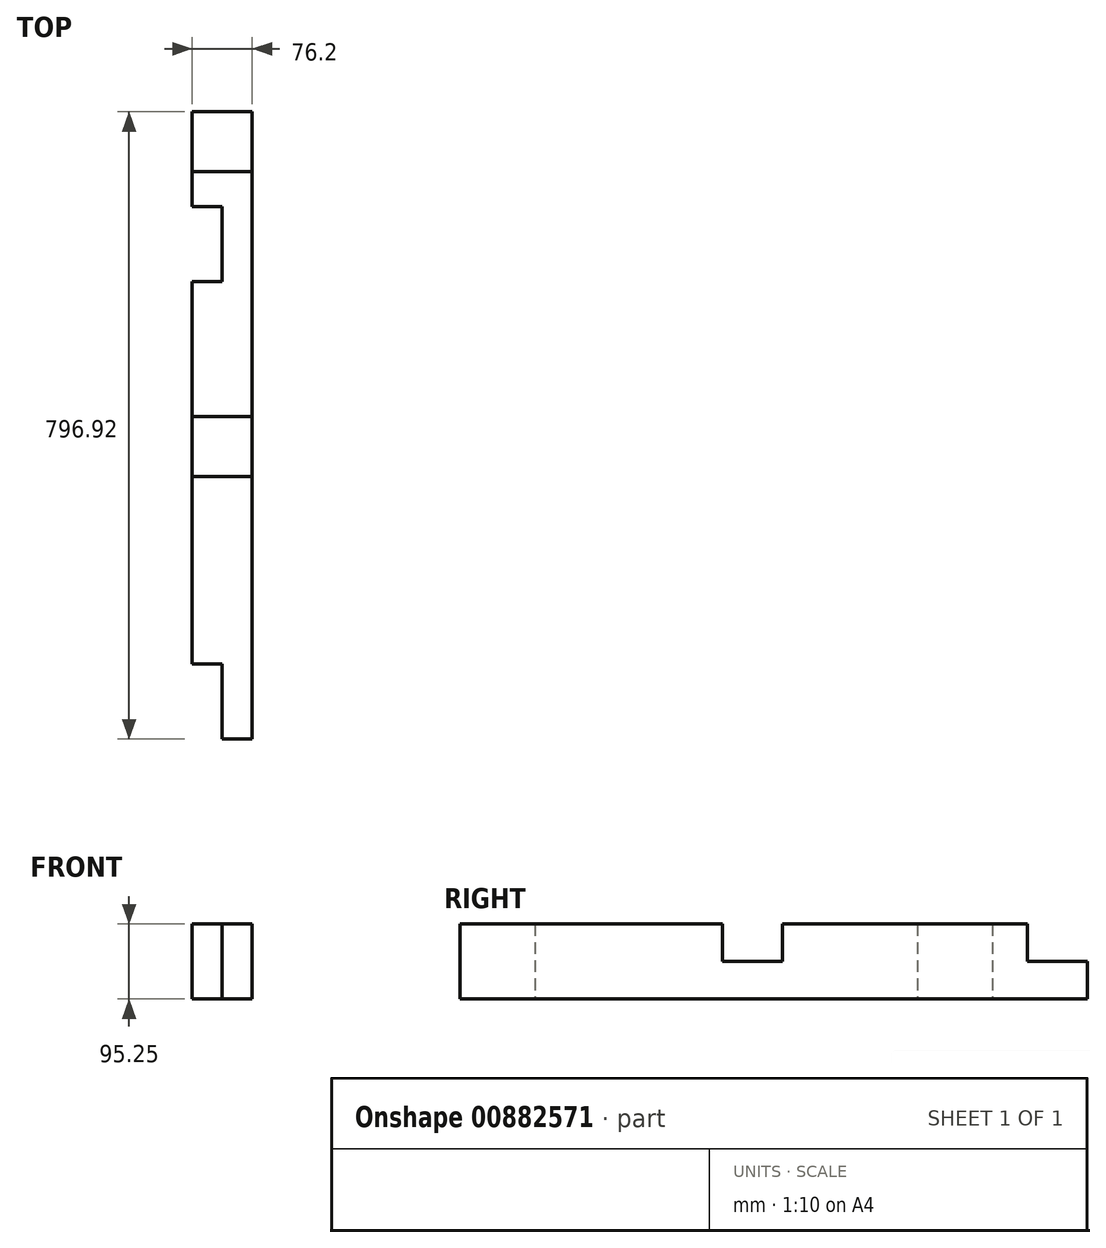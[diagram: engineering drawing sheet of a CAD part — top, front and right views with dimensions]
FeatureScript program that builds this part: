
annotation { "Feature Type Name" : "Feature", "Feature Type Description" : "" }
export const myFeature = defineFeature(function(context is Context, id is Id, definition is map)
    precondition{}
    {
        {
            var Q0;
            Q0=qCreatedBy(makeId("Front.planeOp"),FACE);
            var sketch = newSketch(context, id + "F0", { "sketchPlane" : qUnion([Q0])});
            skLineSegment(sketch, "E0.bottom", {"start": v(0, 0) * mm, "end": v(76.2, 0) * mm});
            skLineSegment(sketch, "E0.top", {"start": v(0, 95.25) * mm, "end": v(76.2, 95.25) * mm});
            skLineSegment(sketch, "E0.left", {"start": v(0, 0) * mm, "end": v(0, 95.25) * mm});
            skLineSegment(sketch, "E0.right", {"start": v(76.2, 0) * mm, "end": v(76.2, 95.25) * mm});
            skSolve(sketch);
        }
        {
            var Q0;
            Q0=qSketchRegion(id+"F0",true);
            extrude(context, id + "F1", {"entities" : qUnion([Q0]), "depth" : 796.92 * mm, "offsetDistance" : 25.4 * mm});
        }
        {
            var Q0;
            Q0=makeQuery(id+"F1.opExtrude","SWEPT_FACE",FACE,{"disambiguationData":[OSD([sQuery(id+"F0.wireOp",EDGE,"E0.right")])]});
            var sketch = newSketch(context, id + "F2", { "sketchPlane" : qUnion([Q0])});
            skLineSegment(sketch, "E1.bottom", {"start": v(-463.55, 95.25) * mm, "end": v(-387.35, 95.25) * mm});
            skLineSegment(sketch, "E1.top", {"start": v(-463.55, 47.62) * mm, "end": v(-387.35, 47.62) * mm});
            skLineSegment(sketch, "E1.left", {"start": v(-463.55, 95.25) * mm, "end": v(-463.55, 47.63) * mm});
            skLineSegment(sketch, "E1.right", {"start": v(-387.35, 95.25) * mm, "end": v(-387.35, 47.63) * mm});
            skLineSegment(sketch, "E2.bottom", {"start": v(-76.2, 95.25) * mm, "end": v(0, 95.25) * mm});
            skLineSegment(sketch, "E2.top", {"start": v(-76.2, 47.62) * mm, "end": v(0, 47.62) * mm});
            skLineSegment(sketch, "E2.left", {"start": v(-76.2, 95.25) * mm, "end": v(-76.2, 47.62) * mm});
            skLineSegment(sketch, "E2.right", {"start": v(0, 95.25) * mm, "end": v(0, 47.62) * mm});
            skSolve(sketch);
        }
        {
            var Q0;
            Q0=qSketchRegion(id+"F2",true);
            extrude(context, id + "F3", {"entities" : qUnion([Q0]), "operationType" : NewBodyOperationType.REMOVE, "endBound" : BoundingType.THROUGH_ALL, "oppositeDirection" : true, "depth" : 25.4 * mm, "offsetDistance" : 25.4 * mm});
        }
        {
            var Q0;
            Q0=makeQuery(id+"F1.opExtrude","SWEPT_FACE",FACE,{"disambiguationData":[OSD([sQuery(id+"F0.wireOp",EDGE,"E0.left")])]});
            var sketch = newSketch(context, id + "F4", { "sketchPlane" : qUnion([Q0])});
            skLineSegment(sketch, "E3.bottom", {"start": v(796.93, 95.25) * mm, "end": v(701.68, 95.25) * mm});
            skLineSegment(sketch, "E3.top", {"start": v(796.93, 0) * mm, "end": v(701.68, 0) * mm});
            skLineSegment(sketch, "E3.left", {"start": v(796.93, 95.25) * mm, "end": v(796.93, 0) * mm});
            skLineSegment(sketch, "E3.right", {"start": v(701.68, 95.25) * mm, "end": v(701.68, 0) * mm});
            skSolve(sketch);
        }
        {
            var Q0;
            Q0 = qSketchRegion(id + "F4", true);
            extrude(context, id + "F5", {"entities" : qUnion([Q0]), "operationType" : NewBodyOperationType.REMOVE, "oppositeDirection" : true, "depth" : 38.1 * mm, "offsetDistance" : 25.4 * mm});
        }
        {
            var Q0;
            Q0=makeQuery(id+"F1.opExtrude","SWEPT_FACE",FACE,{"disambiguationData":[OSD([sQuery(id+"F0.wireOp",EDGE,"E0.left")])]});
            var sketch = newSketch(context, id + "F6", { "sketchPlane" : qUnion([Q0])});
            skLineSegment(sketch, "E4.bottom", {"start": v(120.65, 95.25) * mm, "end": v(215.9, 95.25) * mm});
            skLineSegment(sketch, "E4.top", {"start": v(120.65, 0) * mm, "end": v(215.9, 0) * mm});
            skLineSegment(sketch, "E4.left", {"start": v(120.65, 95.25) * mm, "end": v(120.65, 0) * mm});
            skLineSegment(sketch, "E4.right", {"start": v(215.9, 95.25) * mm, "end": v(215.9, 0) * mm});
            skSolve(sketch);
        }
        {
            var Q0;
            Q0 = qSketchRegion(id + "F6", true);
            extrude(context, id + "F7", {"entities" : qUnion([Q0]), "operationType" : NewBodyOperationType.REMOVE, "oppositeDirection" : true, "depth" : 38.1 * mm, "offsetDistance" : 25.4 * mm});
        }
    });
